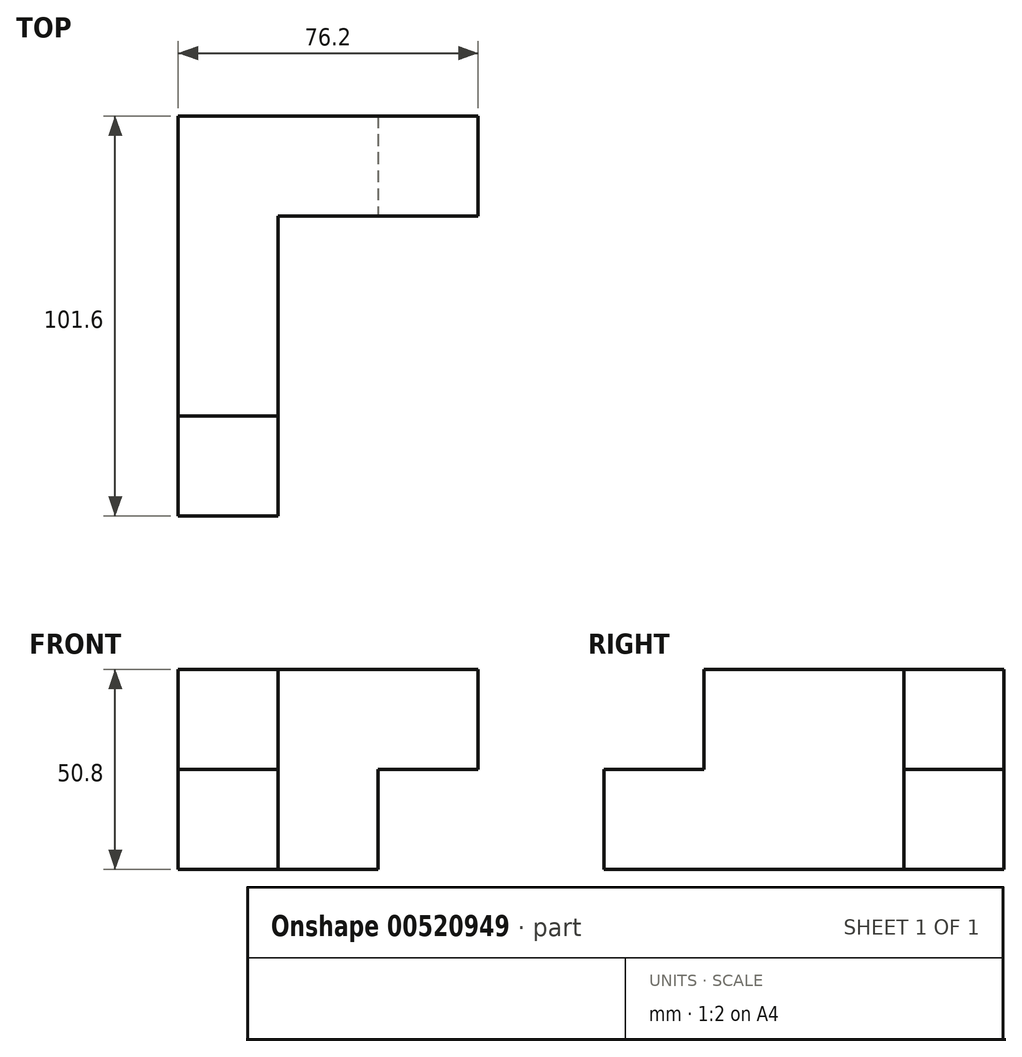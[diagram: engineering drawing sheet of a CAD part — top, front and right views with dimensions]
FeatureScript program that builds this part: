
annotation { "Feature Type Name" : "Feature", "Feature Type Description" : "" }
export const myFeature = defineFeature(function(context is Context, id is Id, definition is map)
    precondition{}
    {
        {
            var Q0;
            Q0=qCreatedBy(makeId("Right.planeOp"),FACE);
            var sketch = newSketch(context, id + "F0", { "sketchPlane" : qUnion([Q0])});
            skLineSegment(sketch, "E0.bottom", {"start": v(0, 0) * mm, "end": v(101.6, 0) * mm});
            skLineSegment(sketch, "E0.top", {"start": v(0, 50.8) * mm, "end": v(101.6, 50.8) * mm});
            skLineSegment(sketch, "E0.left", {"start": v(0, 0) * mm, "end": v(0, 50.8) * mm});
            skLineSegment(sketch, "E0.right", {"start": v(101.6, 0) * mm, "end": v(101.6, 50.8) * mm});
            skSolve(sketch);
        }
        {
            var Q0;
            Q0=makeQuery(id+"F0.imprint","IMPRINT",FACE,{"disambiguationData":[TD([[makeQuery(id+"F0.imprint","IMPRINT",EDGE,{"derivedFrom":sQuery(id+"F0.wireOp",EDGE,"E0.bottom")}),1.0]])]});
            extrude(context, id + "F1", {"entities" : qUnion([Q0]), "depth" : 25.4 * mm, "offsetDistance" : 25.4 * mm});
        }
        {
            var Q0;
            Q0=makeQuery(id+"F1.opExtrude","CAP_FACE",FACE,{"disambiguationData":[OSD([sQuery(id+"F0.wireOp",EDGE,"E0.bottom"),sQuery(id+"F0.wireOp",EDGE,"E0.top"),sQuery(id+"F0.wireOp",EDGE,"E0.left"),sQuery(id+"F0.wireOp",EDGE,"E0.right")])],"isStart":false});
            var sketch = newSketch(context, id + "F2", { "sketchPlane" : qUnion([Q0])});
            skLineSegment(sketch, "E1.bottom", {"start": v(0, 50.8) * mm, "end": v(25.4, 50.8) * mm});
            skLineSegment(sketch, "E1.top", {"start": v(0, 25.4) * mm, "end": v(25.4, 25.4) * mm});
            skLineSegment(sketch, "E1.left", {"start": v(0, 50.8) * mm, "end": v(0, 25.4) * mm});
            skLineSegment(sketch, "E1.right", {"start": v(25.4, 50.8) * mm, "end": v(25.4, 25.4) * mm});
            skSolve(sketch);
        }
        {
            var Q0;
            Q0=makeQuery(id+"F2.imprint","IMPRINT",FACE,{"disambiguationData":[TD([[makeQuery(id+"F2.imprint","IMPRINT",EDGE,{"derivedFrom":sQuery(id+"F2.wireOp",EDGE,"E1.bottom")}),-1.0]])]});
            extrude(context, id + "F3", {"entities" : qUnion([Q0]), "operationType" : NewBodyOperationType.REMOVE, "oppositeDirection" : true, "depth" : 25.4 * mm, "offsetDistance" : 25.4 * mm});
        }
        {
            var Q0;
            Q0=makeQuery(id+"F1.opExtrude","CAP_FACE",FACE,{"disambiguationData":[OSD([sQuery(id+"F0.wireOp",EDGE,"E0.bottom"),sQuery(id+"F0.wireOp",EDGE,"E0.top"),sQuery(id+"F0.wireOp",EDGE,"E0.left"),sQuery(id+"F0.wireOp",EDGE,"E0.right")])],"isStart":false});
            var sketch = newSketch(context, id + "F4", { "sketchPlane" : qUnion([Q0])});
            skLineSegment(sketch, "E2.bottom", {"start": v(101.6, 50.8) * mm, "end": v(76.2, 50.8) * mm});
            skLineSegment(sketch, "E2.top", {"start": v(101.6, 0) * mm, "end": v(76.2, 0) * mm});
            skLineSegment(sketch, "E2.left", {"start": v(101.6, 50.8) * mm, "end": v(101.6, 0) * mm});
            skLineSegment(sketch, "E2.right", {"start": v(76.2, 50.8) * mm, "end": v(76.2, 0) * mm});
            skSolve(sketch);
        }
        {
            var Q0;
            Q0=makeQuery(id+"F4.imprint","IMPRINT",FACE,{"disambiguationData":[TD([[makeQuery(id+"F4.imprint","IMPRINT",EDGE,{"derivedFrom":sQuery(id+"F4.wireOp",EDGE,"E2.bottom")}),-1.0]])]});
            extrude(context, id + "F5", {"entities" : qUnion([Q0]), "operationType" : NewBodyOperationType.ADD, "depth" : 25.4 * mm, "offsetDistance" : 25.4 * mm});
        }
        {
            var Q0;
            Q0=makeQuery(id+"F5.opExtrude","CAP_FACE",FACE,{"disambiguationData":[OSD([sQuery(id+"F4.wireOp",EDGE,"E2.bottom"),sQuery(id+"F4.wireOp",EDGE,"E2.top"),sQuery(id+"F4.wireOp",EDGE,"E2.left"),sQuery(id+"F4.wireOp",EDGE,"E2.right")])],"isStart":false});
            var sketch = newSketch(context, id + "F6", { "sketchPlane" : qUnion([Q0])});
            skLineSegment(sketch, "E3.bottom", {"start": v(101.6, 50.8) * mm, "end": v(76.2, 50.8) * mm});
            skLineSegment(sketch, "E3.top", {"start": v(101.6, 25.4) * mm, "end": v(76.2, 25.4) * mm});
            skLineSegment(sketch, "E3.left", {"start": v(101.6, 50.8) * mm, "end": v(101.6, 25.4) * mm});
            skLineSegment(sketch, "E3.right", {"start": v(76.2, 50.8) * mm, "end": v(76.2, 25.4) * mm});
            skSolve(sketch);
        }
        {
            var Q0;
            Q0=makeQuery(id+"F6.imprint","IMPRINT",FACE,{"disambiguationData":[TD([[makeQuery(id+"F6.imprint","IMPRINT",EDGE,{"derivedFrom":sQuery(id+"F6.wireOp",EDGE,"E3.bottom")}),-1.0]])]});
            extrude(context, id + "F7", {"entities" : qUnion([Q0]), "operationType" : NewBodyOperationType.ADD, "depth" : 25.4 * mm, "offsetDistance" : 25.4 * mm});
        }
    });
